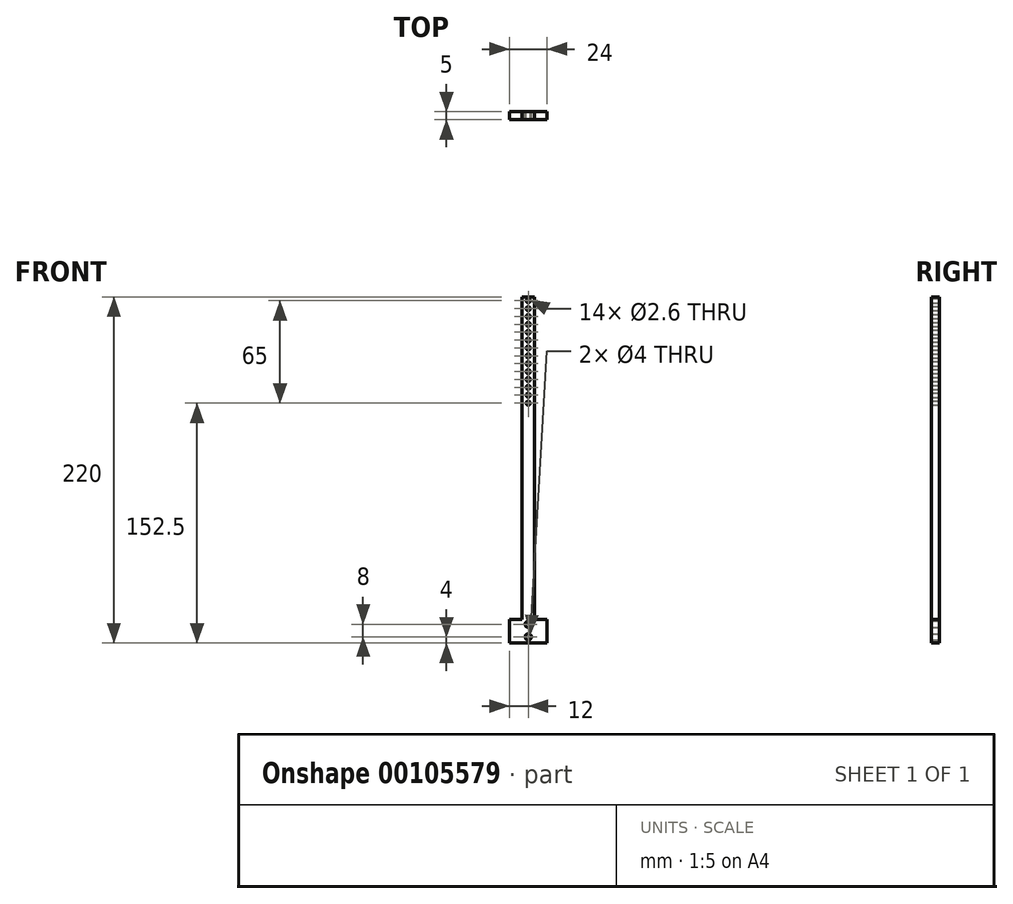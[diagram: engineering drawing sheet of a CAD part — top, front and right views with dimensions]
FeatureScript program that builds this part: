
annotation { "Feature Type Name" : "Feature", "Feature Type Description" : "" }
export const myFeature = defineFeature(function(context is Context, id is Id, definition is map)
    precondition{}
    {
        {
            var Q0;
            Q0=qCreatedBy(makeId("Front.planeOp"),FACE);
            var sketch = newSketch(context, id + "F0", { "sketchPlane" : qUnion([Q0])});
            skLineSegment(sketch, "E0.bottom", {"start": v(4, -125) * mm, "end": v(-4, -125) * mm});
            skLineSegment(sketch, "E0.left", {"start": v(4, -110) * mm, "end": v(4, 95) * mm});
            skLineSegment(sketch, "E0.right", {"start": v(-4, -110) * mm, "end": v(-4, 95) * mm});
            skPoint(sketch, "E0.middle", {"position": v(0, 0) * mm});
            skCircle(sketch, "E1", {"center": v(0, -121) * mm, "radius": 2 * mm});
            skCircle(sketch, "E2", {"center": v(0, -113) * mm, "radius": 2 * mm});
            skCircle(sketch, "E3.0.3.0", {"center": v(0, 87.5) * mm, "radius": 1.3 * mm});
            skCircle(sketch, "E3.0.3.1", {"center": v(0, 92.5) * mm, "radius": 1.3 * mm});
            skCircle(sketch, "E3.0.4.0", {"center": v(0, 77.5) * mm, "radius": 1.3 * mm});
            skCircle(sketch, "E3.0.4.1", {"center": v(0, 82.5) * mm, "radius": 1.3 * mm});
            skCircle(sketch, "E3.0.5.0", {"center": v(0, 67.5) * mm, "radius": 1.3 * mm});
            skCircle(sketch, "E3.0.5.1", {"center": v(0, 72.5) * mm, "radius": 1.3 * mm});
            skCircle(sketch, "E3.0.6.0", {"center": v(0, 57.5) * mm, "radius": 1.3 * mm});
            skCircle(sketch, "E3.0.6.1", {"center": v(0, 62.5) * mm, "radius": 1.3 * mm});
            skCircle(sketch, "E3.0.7.0", {"center": v(0, 47.5) * mm, "radius": 1.3 * mm});
            skCircle(sketch, "E3.0.7.1", {"center": v(0, 52.5) * mm, "radius": 1.3 * mm});
            skCircle(sketch, "E3.0.8.0", {"center": v(0, 37.5) * mm, "radius": 1.3 * mm});
            skCircle(sketch, "E3.0.8.1", {"center": v(0, 42.5) * mm, "radius": 1.3 * mm});
            skCircle(sketch, "E3.0.9.0", {"center": v(0, 27.5) * mm, "radius": 1.3 * mm});
            skCircle(sketch, "E3.0.9.1", {"center": v(0, 32.5) * mm, "radius": 1.3 * mm});
            skLineSegment(sketch, "E4", {"start": v(-4, 95) * mm, "end": v(4, 95) * mm});
            skPoint(sketch, "E5.orphan", {"position": v(-4, 125) * mm});
            skPoint(sketch, "E6.trimOffspring.end.orphan", {"position": v(4, 125) * mm});
            skLineSegment(sketch, "E7.bottom", {"start": v(12, -125) * mm, "end": v(-12, -125) * mm});
            skLineSegment(sketch, "E7.top", {"start": v(12, -110) * mm, "end": v(4, -110) * mm});
            skLineSegment(sketch, "E7.left", {"start": v(12, -125) * mm, "end": v(12, -110) * mm});
            skLineSegment(sketch, "E7.right", {"start": v(-12, -125) * mm, "end": v(-12, -110) * mm});
            skLineSegment(sketch, "E8.trimOffspring", {"start": v(-4, -110) * mm, "end": v(-12, -110) * mm});
            skSolve(sketch);
        }
        {
            var Q0;
            Q0=makeQuery(id+"F0.imprint","IMPRINT",FACE,{"disambiguationData":[TD([[makeQuery(id+"F0.imprint","IMPRINT",EDGE,{"derivedFrom":sQuery(id+"F0.wireOp",EDGE,"E0.left")}),1.0]])]});
            extrude(context, id + "F1", {"entities" : qUnion([Q0]), "depth" : 5 * mm});
        }
    });
